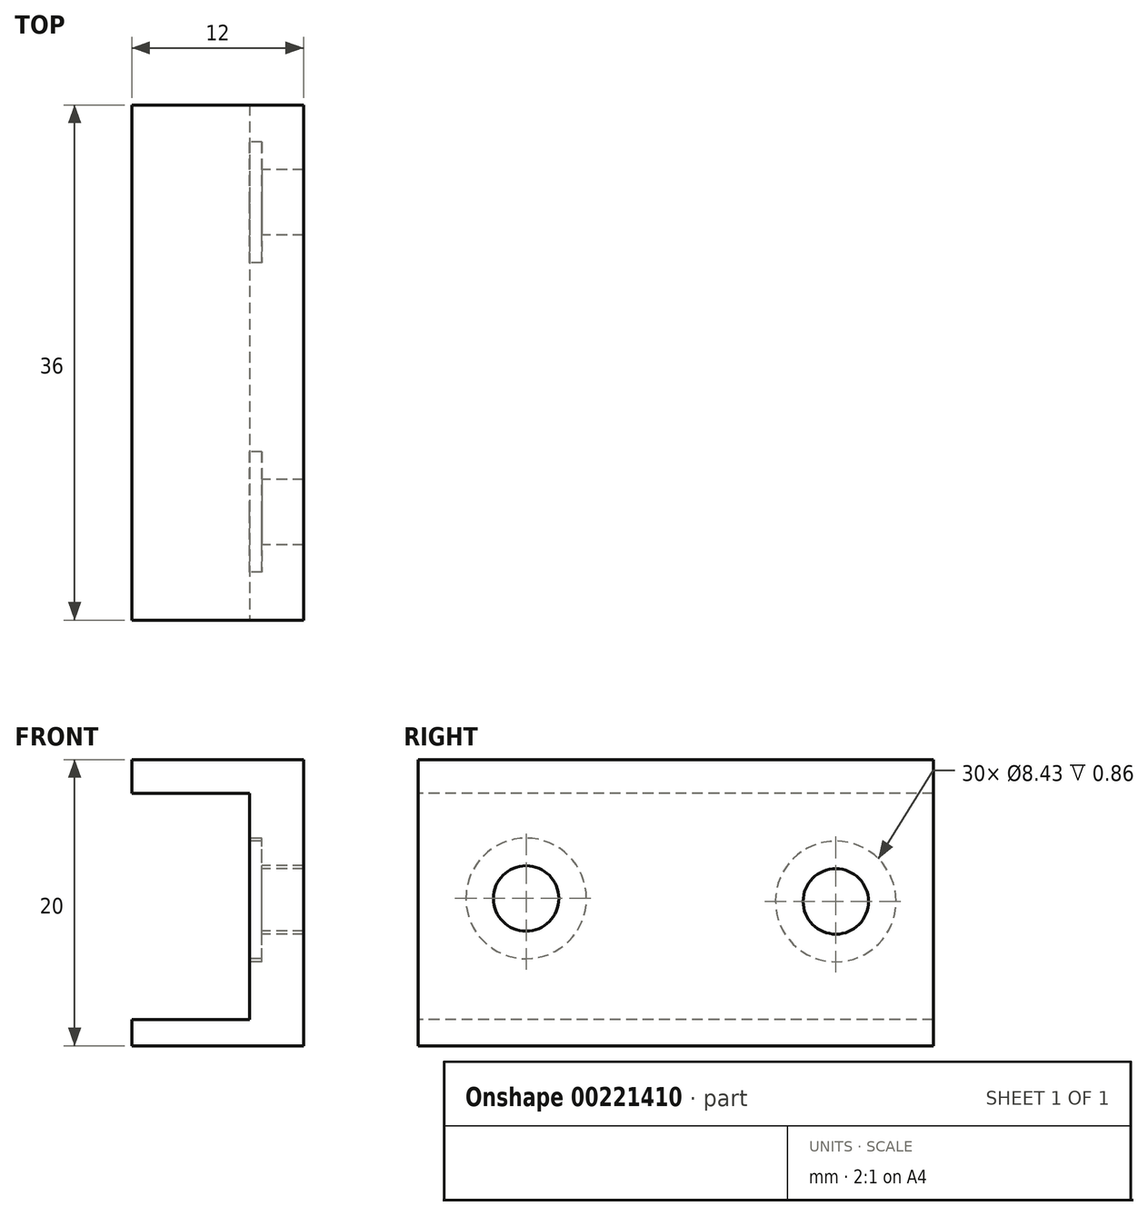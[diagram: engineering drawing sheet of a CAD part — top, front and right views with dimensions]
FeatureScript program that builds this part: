
annotation { "Feature Type Name" : "Feature", "Feature Type Description" : "" }
export const myFeature = defineFeature(function(context is Context, id is Id, definition is map)
    precondition{}
    {
        {
            var Q0;
            Q0=qCreatedBy(makeId("Right.planeOp"),FACE);
            var sketch = newSketch(context, id + "F0", { "sketchPlane" : qUnion([Q0])});
            skLineSegment(sketch, "E0.bottom", {"start": v(-66.51, 25.17) * mm, "end": v(-30.51, 25.17) * mm});
            skLineSegment(sketch, "E0.top", {"start": v(-66.51, 5.17) * mm, "end": v(-30.51, 5.17) * mm});
            skLineSegment(sketch, "E0.left", {"start": v(-66.51, 25.17) * mm, "end": v(-66.51, 5.17) * mm});
            skLineSegment(sketch, "E0.right", {"start": v(-30.51, 25.17) * mm, "end": v(-30.51, 5.17) * mm});
            skSolve(sketch);
        }
        {
            var Q0;
            Q0=makeQuery(id+"F0.imprint","IMPRINT",FACE,{"disambiguationData":[TD([[makeQuery(id+"F0.imprint","IMPRINT",EDGE,{"derivedFrom":sQuery(id+"F0.wireOp",EDGE,"E0.bottom")}),-1.0]])]});
            extrude(context, id + "F1", {"entities" : qUnion([Q0]), "depth" : 12 * mm});
        }
        {
            var Q0;
            Q0=qCreatedBy(makeId("Right.planeOp"),FACE);
            var sketch = newSketch(context, id + "F2", { "sketchPlane" : qUnion([Q0])});
            skLineSegment(sketch, "E1.bottom", {"start": v(-26.56, 22.8) * mm, "end": v(-70.31, 22.8) * mm});
            skLineSegment(sketch, "E1.top", {"start": v(-26.56, 7) * mm, "end": v(-70.31, 7) * mm});
            skLineSegment(sketch, "E1.left", {"start": v(-26.56, 22.8) * mm, "end": v(-26.56, 7) * mm});
            skLineSegment(sketch, "E1.right", {"start": v(-70.31, 22.8) * mm, "end": v(-70.31, 7) * mm});
            skSolve(sketch);
        }
        {
            var Q0;
            Q0=makeQuery(id+"F2.imprint","IMPRINT",FACE,{"disambiguationData":[TD([[makeQuery(id+"F2.imprint","IMPRINT",EDGE,{"derivedFrom":sQuery(id+"F2.wireOp",EDGE,"E1.bottom")}),1.0]])]});
            extrude(context, id + "F3", {"entities" : qUnion([Q0]), "operationType" : NewBodyOperationType.REMOVE, "depth" : 8.24 * mm});
        }
        {
            var Q0;
            Q0=qCreatedBy(makeId("Right.planeOp"),FACE);
            var sketch = newSketch(context, id + "F4", { "sketchPlane" : qUnion([Q0])});
            skCircle(sketch, "E2", {"center": v(-37.32, 15.26) * mm, "radius": 2.29 * mm});
            skCircle(sketch, "E3", {"center": v(-58.96, 15.46) * mm, "radius": 2.29 * mm});
            skSolve(sketch);
        }
        {
            var Q0;
            Q0 = qSketchRegion(id + "F4", true);
            extrude(context, id + "F5", {"entities" : qUnion([Q0]), "operationType" : NewBodyOperationType.REMOVE, "depth" : 34.9 * mm});
        }
        {
            var Q0;
            Q0=qCreatedBy(makeId("Right.planeOp"),FACE);
            var sketch = newSketch(context, id + "F6", { "sketchPlane" : qUnion([Q0])});
            skCircle(sketch, "E4", {"center": v(-37.32, 15.26) * mm, "radius": 4.21 * mm});
            skCircle(sketch, "E5", {"center": v(-58.96, 15.46) * mm, "radius": 4.21 * mm});
            skSolve(sketch);
        }
        {
            var Q0;
            Q0 = qSketchRegion(id + "F6", true);
            extrude(context, id + "F7", {"entities" : qUnion([Q0]), "operationType" : NewBodyOperationType.REMOVE, "depth" : 9.1 * mm});
        }
    });
